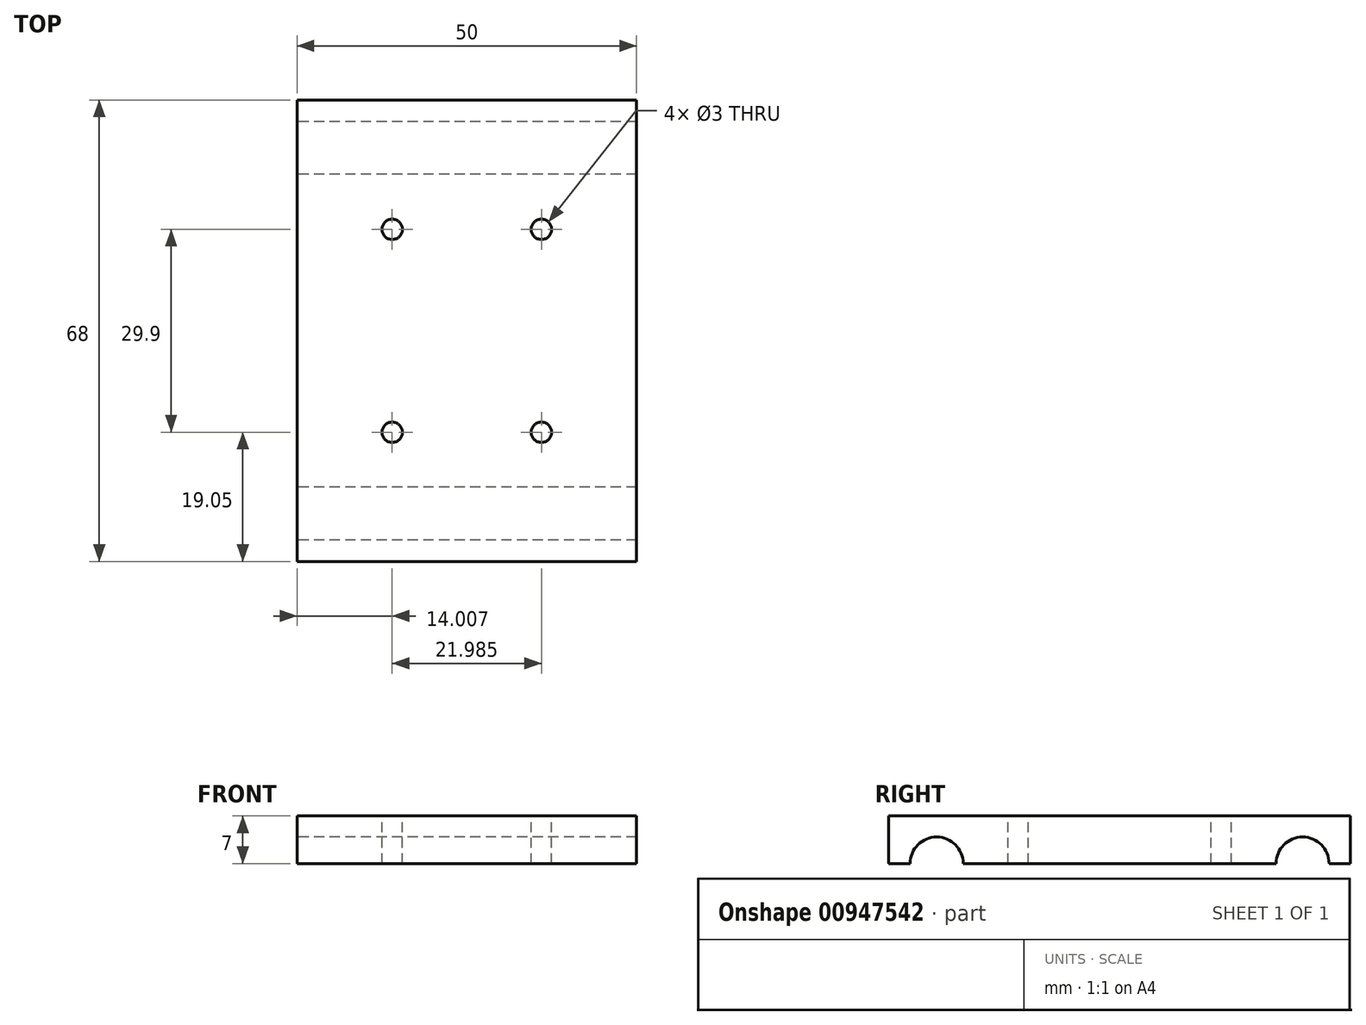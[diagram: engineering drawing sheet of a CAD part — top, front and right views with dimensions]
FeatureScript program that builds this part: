
annotation { "Feature Type Name" : "Feature", "Feature Type Description" : "" }
export const myFeature = defineFeature(function(context is Context, id is Id, definition is map)
    precondition{}
    {
        {
            var Q0;
            Q0=qCreatedBy(makeId("Right.planeOp"),FACE);
            var sketch = newSketch(context, id + "F0", { "sketchPlane" : qUnion([Q0])});
            skLineSegment(sketch, "E0.top", {"start": v(34, 7) * mm, "end": v(-34, 7) * mm});
            skLineSegment(sketch, "E0.left", {"start": v(34, 0) * mm, "end": v(34, 7) * mm});
            skLineSegment(sketch, "E0.right", {"start": v(-34, 0) * mm, "end": v(-34, 7) * mm});
            skPoint(sketch, "E0.middle", {"position": v(0, 0) * mm});
            skLineSegment(sketch, "E1", {"start": v(0, 0) * mm, "end": v(23.05, 0) * mm, "construction": true});
            skArc(sketch, "E2", {"start": v(30.85, 0) * mm, "mid": v(26.95, 3.9) * mm, "end": v(23.05, 0) * mm});
            skLineSegment(sketch, "E3", {"start": v(0, 7) * mm, "end": v(0, -7) * mm, "construction": true});
            skArc(sketch, "E4.MirrorC", {"start": v(-30.85, 0) * mm, "mid": v(-26.95, 3.9) * mm, "end": v(-23.05, 0) * mm});
            skLineSegment(sketch, "E5", {"start": v(-34, 0) * mm, "end": v(-30.85, 0) * mm});
            skPoint(sketch, "E6.orphan", {"position": v(-34, -7) * mm});
            skPoint(sketch, "E7.orphan", {"position": v(34, -7) * mm});
            skLineSegment(sketch, "E8.trimOffspring", {"start": v(-23.05, 0) * mm, "end": v(23.05, 0) * mm});
            skLineSegment(sketch, "E9.trimOffspring", {"start": v(30.85, 0) * mm, "end": v(34, 0) * mm});
            skSolve(sketch);
        }
        {
            var Q0;
            Q0 = qSketchRegion(id + "F0", true);
            extrude(context, id + "F1", {"entities" : qUnion([Q0]), "depth" : 50 * mm, "offsetDistance" : 25 * mm});
        }
        {
            var Q0;
            Q0=makeQuery(id+"F1.opExtrude","SWEPT_FACE",FACE,{"disambiguationData":[OSD([sQuery(id+"F0.wireOp",EDGE,"E0.top")])]});
            var sketch = newSketch(context, id + "F2", { "sketchPlane" : qUnion([Q0])});
            skLineSegment(sketch, "E10", {"start": v(0, 34) * mm, "end": v(50, -34) * mm, "construction": true});
            skLineSegment(sketch, "E11", {"start": v(0, -34) * mm, "end": v(50, 34) * mm, "construction": true});
            skLineSegment(sketch, "E12.bottom", {"start": v(40, 14.95) * mm, "end": v(10, 14.95) * mm, "construction": true});
            skLineSegment(sketch, "E12.top", {"start": v(40, -14.95) * mm, "end": v(10, -14.95) * mm, "construction": true});
            skLineSegment(sketch, "E12.left", {"start": v(40, 14.95) * mm, "end": v(40, -14.95) * mm, "construction": true});
            skLineSegment(sketch, "E12.right", {"start": v(10, 14.95) * mm, "end": v(10, -14.95) * mm, "construction": true});
            skPoint(sketch, "E12.middle", {"position": v(25, 0) * mm});
            skPoint(sketch, "E13", {"position": v(14, 14.95) * mm});
            skPoint(sketch, "E14", {"position": v(36, 14.95) * mm});
            skPoint(sketch, "E15", {"position": v(14, -14.95) * mm});
            skPoint(sketch, "E16", {"position": v(36, -14.95) * mm});
            skSolve(sketch);
        }
        {
            var Q0;
            Q0=sQuery(id+"F2.wireOp",VERTEX,"E13");
            var Q1;
            Q1=sQuery(id+"F2.wireOp",VERTEX,"E14");
            var Q2;
            Q2=sQuery(id+"F2.wireOp",VERTEX,"E15");
            var Q3;
            Q3=sQuery(id+"F2.wireOp",VERTEX,"E16");
            var Q4;
            Q4=makeQuery(id+"F1.opExtrude","SWEPT_BODY",BODY,{"disambiguationData":[OSD([sQuery(id+"F0.wireOp",EDGE,"E0.bottom"),sQuery(id+"F0.wireOp",EDGE,"E0.top"),sQuery(id+"F0.wireOp",EDGE,"E0.left"),sQuery(id+"F0.wireOp",EDGE,"E0.right"),sQuery(id+"F0.wireOp",EDGE,"E2"),sQuery(id+"F0.wireOp",EDGE,"E4.MirrorC")])]});
            hole(context, id + "F3", {"style" : HoleStyle.SIMPLE, "endStyle" : HoleEndStyle.THROUGH, "holeDiameter" : 3 * mm, "majorDiameter" : 5 * mm, "isTappedThrough" : true, "tappedDepth" : 12 * mm, "tapClearance" : 3, "locations" : qUnion([Q0, Q1, Q2, Q3]), "scope" : qUnion([Q4])});
        }
    });
